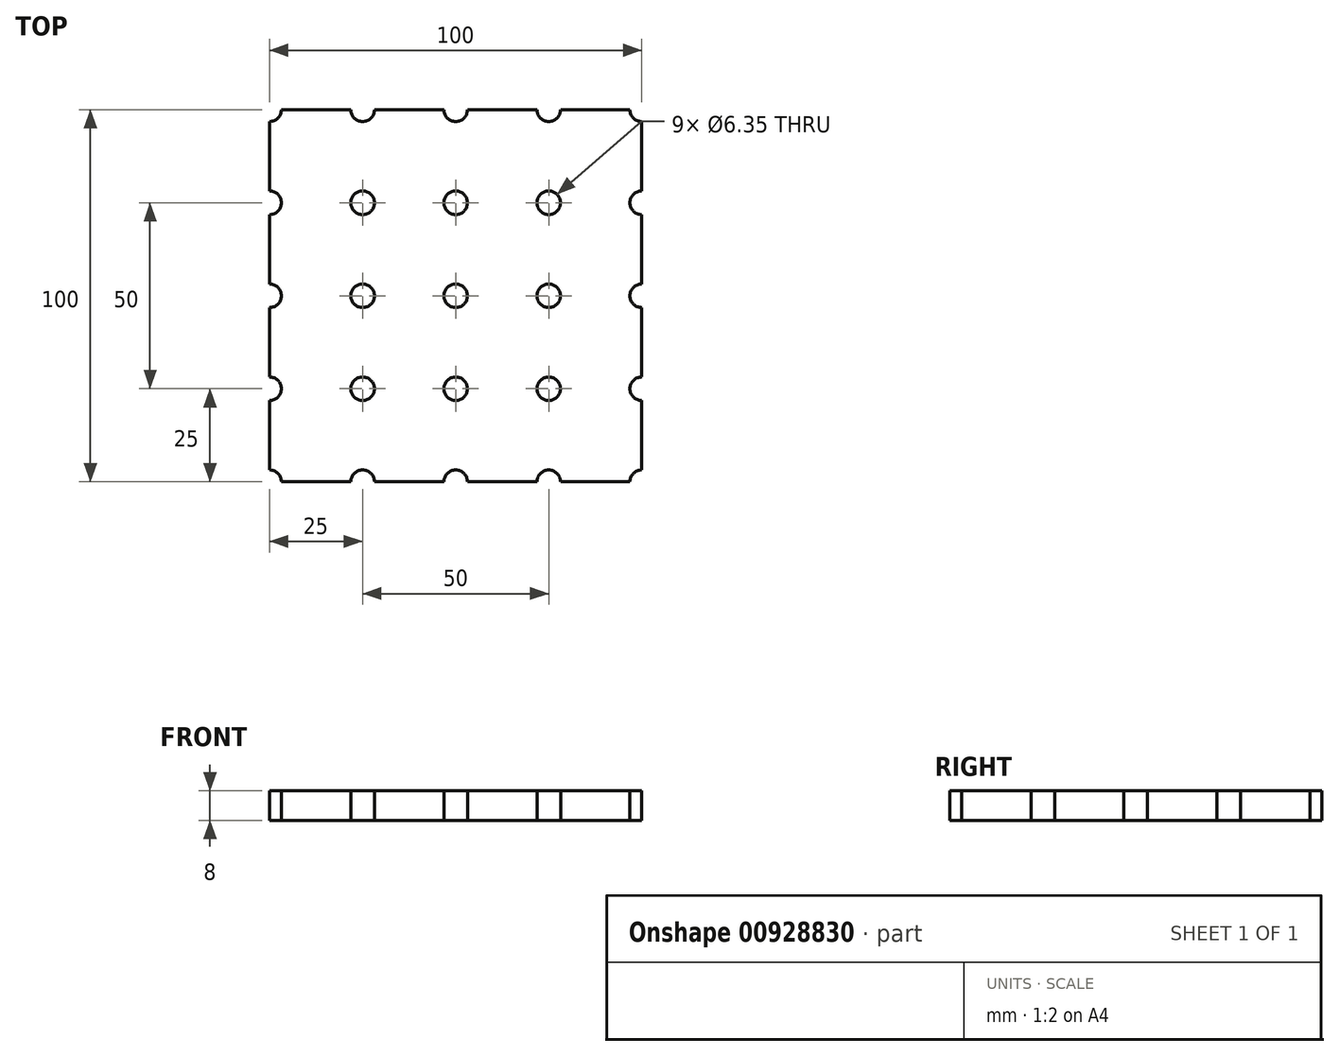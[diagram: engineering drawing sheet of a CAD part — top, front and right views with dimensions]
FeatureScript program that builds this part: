
annotation { "Feature Type Name" : "Feature", "Feature Type Description" : "" }
export const myFeature = defineFeature(function(context is Context, id is Id, definition is map)
    precondition{}
    {
        {
            var Q0;
            Q0=qCreatedBy(makeId("Top.planeOp"),FACE);
            var sketch = newSketch(context, id + "F0", { "sketchPlane" : qUnion([Q0])});
            skLineSegment(sketch, "E0.bottom", {"start": v(-50, -50) * mm, "end": v(50, -50) * mm});
            skLineSegment(sketch, "E0.top", {"start": v(-50, 50) * mm, "end": v(50, 50) * mm});
            skLineSegment(sketch, "E0.left", {"start": v(-50, -50) * mm, "end": v(-50, 50) * mm});
            skLineSegment(sketch, "E0.right", {"start": v(50, -50) * mm, "end": v(50, 50) * mm});
            skPoint(sketch, "E0.middle", {"position": v(0, 0) * mm});
            skCircle(sketch, "E1", {"center": v(-50, 50) * mm, "radius": 3.17 * mm});
            skCircle(sketch, "E2.0.1.0", {"center": v(-50, 25) * mm, "radius": 3.17 * mm});
            skCircle(sketch, "E2.0.2.0", {"center": v(-50, 0) * mm, "radius": 3.17 * mm});
            skCircle(sketch, "E2.0.3.0", {"center": v(-50, -25) * mm, "radius": 3.17 * mm});
            skCircle(sketch, "E2.0.4.0", {"center": v(-50, -50) * mm, "radius": 3.17 * mm});
            skCircle(sketch, "E2.1.0.0", {"center": v(-25, 50) * mm, "radius": 3.17 * mm});
            skCircle(sketch, "E2.1.1.0", {"center": v(-25, 25) * mm, "radius": 3.17 * mm});
            skCircle(sketch, "E2.1.2.0", {"center": v(-25, 0) * mm, "radius": 3.17 * mm});
            skCircle(sketch, "E2.1.3.0", {"center": v(-25, -25) * mm, "radius": 3.17 * mm});
            skCircle(sketch, "E2.1.4.0", {"center": v(-25, -50) * mm, "radius": 3.17 * mm});
            skCircle(sketch, "E2.2.0.0", {"center": v(0, 50) * mm, "radius": 3.17 * mm});
            skCircle(sketch, "E2.2.1.0", {"center": v(0, 25) * mm, "radius": 3.17 * mm});
            skCircle(sketch, "E2.2.2.0", {"center": v(0, 0) * mm, "radius": 3.17 * mm});
            skCircle(sketch, "E2.2.3.0", {"center": v(0, -25) * mm, "radius": 3.17 * mm});
            skCircle(sketch, "E2.2.4.0", {"center": v(0, -50) * mm, "radius": 3.17 * mm});
            skCircle(sketch, "E2.3.0.0", {"center": v(25, 50) * mm, "radius": 3.17 * mm});
            skCircle(sketch, "E2.3.1.0", {"center": v(25, 25) * mm, "radius": 3.17 * mm});
            skCircle(sketch, "E2.3.2.0", {"center": v(25, 0) * mm, "radius": 3.17 * mm});
            skCircle(sketch, "E2.3.3.0", {"center": v(25, -25) * mm, "radius": 3.17 * mm});
            skCircle(sketch, "E2.3.4.0", {"center": v(25, -50) * mm, "radius": 3.17 * mm});
            skCircle(sketch, "E2.4.0.0", {"center": v(50, 50) * mm, "radius": 3.17 * mm});
            skCircle(sketch, "E2.4.1.0", {"center": v(50, 25) * mm, "radius": 3.17 * mm});
            skCircle(sketch, "E2.4.2.0", {"center": v(50, 0) * mm, "radius": 3.17 * mm});
            skCircle(sketch, "E2.4.3.0", {"center": v(50, -25) * mm, "radius": 3.17 * mm});
            skCircle(sketch, "E2.4.4.0", {"center": v(50, -50) * mm, "radius": 3.17 * mm});
            skLineSegment(sketch, "E2.direction1", {"start": v(-50, 50) * mm, "end": v(-25, 50) * mm, "construction": true});
            skLineSegment(sketch, "E2.direction2", {"start": v(-50, 50) * mm, "end": v(-50, 25) * mm, "construction": true});
            skSolve(sketch);
        }
        {
            var Q0;
            Q0=makeQuery(id+"F0.imprint","IMPRINT",FACE,{"disambiguationData":[TD([[makeQuery(id+"F0.imprint","IMPRINT",EDGE,{"derivedFrom":sQuery(id+"F0.wireOp",EDGE,"E2.1.1.0")}),-1.0]])]});
            extrude(context, id + "F1", {"entities" : qUnion([Q0]), "depth" : 8 * mm, "offsetDistance" : 25 * mm});
        }
    });
